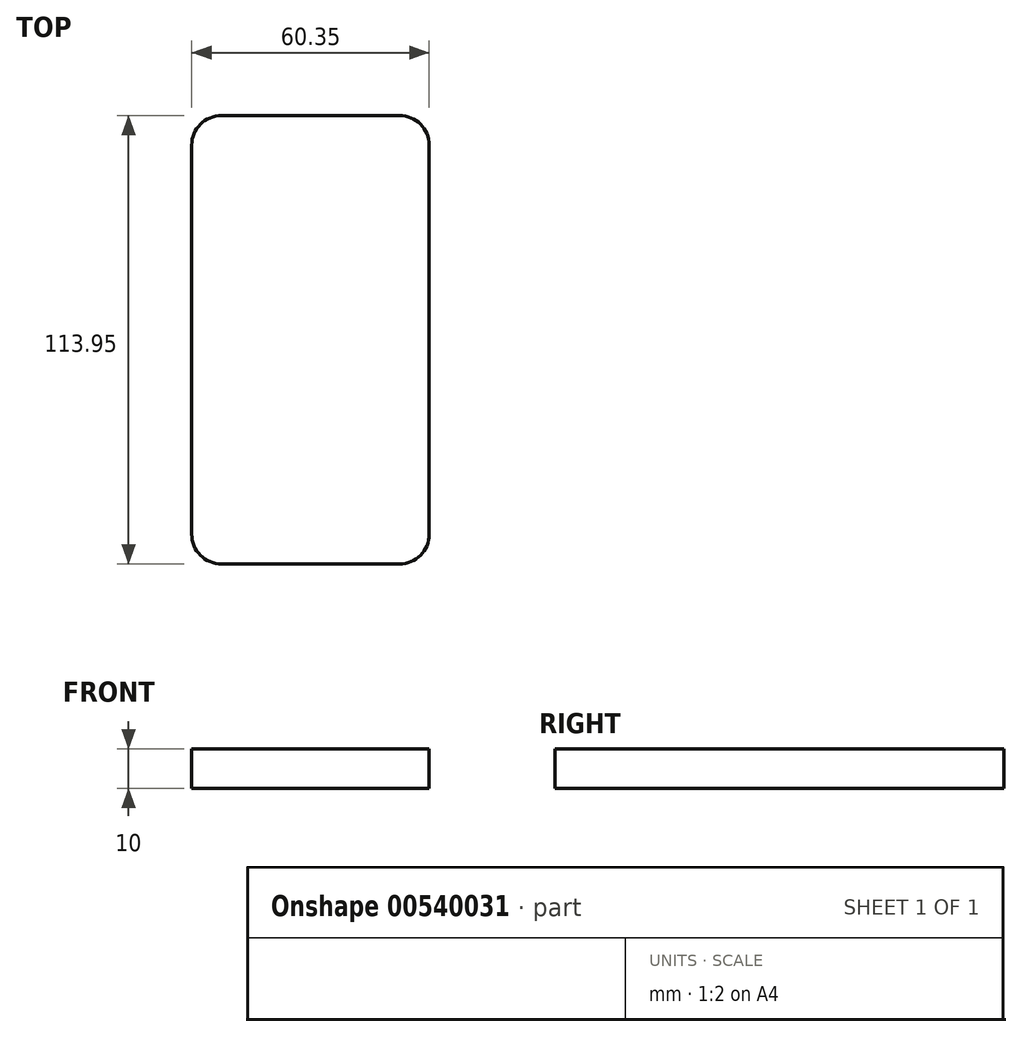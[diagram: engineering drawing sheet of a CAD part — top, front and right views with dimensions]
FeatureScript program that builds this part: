
annotation { "Feature Type Name" : "Feature", "Feature Type Description" : "" }
export const myFeature = defineFeature(function(context is Context, id is Id, definition is map)
    precondition{}
    {
        {
            var Q0;
            Q0=qCreatedBy(makeId("Top.planeOp"),FACE);
            var sketch = newSketch(context, id + "F0", { "sketchPlane" : qUnion([Q0])});
            skLineSegment(sketch, "E0.bottom", {"start": v(-64.28, 31.72) * mm, "end": v(-19.07, 31.72) * mm});
            skLineSegment(sketch, "E0.top", {"start": v(-64.28, -82.23) * mm, "end": v(-19.07, -82.23) * mm});
            skLineSegment(sketch, "E0.left", {"start": v(-71.85, 24.15) * mm, "end": v(-71.85, -74.66) * mm});
            skLineSegment(sketch, "E0.right", {"start": v(-11.5, 24.15) * mm, "end": v(-11.5, -74.66) * mm});
            skPoint(sketch, "E0.middle", {"position": v(-41.68, -25.25) * mm});
            skPoint(sketch, "E1.visualSharp", {"position": v(-71.85, 31.72) * mm});
            skArc(sketch, "E1.filletArc", {"start": v(-64.28, 31.72) * mm, "mid": v(-69.64, 29.5) * mm, "end": v(-71.85, 24.15) * mm});
            skPoint(sketch, "E2.visualSharp", {"position": v(-11.5, 31.72) * mm});
            skArc(sketch, "E2.filletArc", {"start": v(-11.5, 24.15) * mm, "mid": v(-13.72, 29.5) * mm, "end": v(-19.07, 31.72) * mm});
            skPoint(sketch, "E3.visualSharp", {"position": v(-71.85, -82.23) * mm});
            skArc(sketch, "E3.filletArc", {"start": v(-71.85, -74.66) * mm, "mid": v(-69.64, -80) * mm, "end": v(-64.28, -82.23) * mm});
            skPoint(sketch, "E4.visualSharp", {"position": v(-11.5, -82.23) * mm});
            skArc(sketch, "E4.filletArc", {"start": v(-19.07, -82.23) * mm, "mid": v(-13.72, -80) * mm, "end": v(-11.5, -74.66) * mm});
            skCircle(sketch, "E5", {"center": v(-41.68, -72.47) * mm, "radius": 5.6 * mm});
            skLineSegment(sketch, "E6.bottom", {"start": v(-37.43, 20.62) * mm, "end": v(-45.93, 20.62) * mm});
            skLineSegment(sketch, "E6.top", {"start": v(-37.43, 23.32) * mm, "end": v(-45.93, 23.32) * mm});
            skLineSegment(sketch, "E6.left", {"start": v(-36.08, 21.97) * mm, "end": v(-36.08, 21.97) * mm});
            skLineSegment(sketch, "E6.right", {"start": v(-47.28, 21.97) * mm, "end": v(-47.28, 21.97) * mm});
            skPoint(sketch, "E6.middle", {"position": v(-41.68, 21.97) * mm});
            skPoint(sketch, "E7.visualSharp", {"position": v(-47.28, 23.32) * mm});
            skArc(sketch, "E7.filletArc", {"start": v(-45.93, 23.32) * mm, "mid": v(-46.88, 22.93) * mm, "end": v(-47.28, 21.97) * mm});
            skPoint(sketch, "E8.visualSharp", {"position": v(-47.28, 20.62) * mm});
            skArc(sketch, "E8.filletArc", {"start": v(-47.28, 21.97) * mm, "mid": v(-46.88, 21.02) * mm, "end": v(-45.93, 20.62) * mm});
            skPoint(sketch, "E9.visualSharp", {"position": v(-36.08, 20.62) * mm});
            skArc(sketch, "E9.filletArc", {"start": v(-37.43, 20.62) * mm, "mid": v(-36.47, 21.02) * mm, "end": v(-36.08, 21.97) * mm});
            skPoint(sketch, "E10.visualSharp", {"position": v(-36.08, 23.32) * mm});
            skArc(sketch, "E10.filletArc", {"start": v(-36.08, 21.97) * mm, "mid": v(-36.47, 22.93) * mm, "end": v(-37.43, 23.32) * mm});
            skPoint(sketch, "E11.endSnap0", {"position": v(-41.68, 20.62) * mm});
            skPoint(sketch, "E12.middle", {"position": v(-41.68, 26.07) * mm});
            skLineSegment(sketch, "E13.left", {"start": v(-38.75, 26.07) * mm, "end": v(-38.75, 26.07) * mm});
            skLineSegment(sketch, "E14.MirrorCS", {"start": v(-44.6, 26.07) * mm, "end": v(-44.6, 26.07) * mm});
            skLineSegment(sketch, "E15", {"start": v(-44, 26.67) * mm, "end": v(-39.35, 26.67) * mm});
            skLineSegment(sketch, "E16", {"start": v(-39.35, 25.47) * mm, "end": v(-44, 25.47) * mm});
            skPoint(sketch, "E17.visualSharp", {"position": v(-44.6, 26.67) * mm});
            skArc(sketch, "E17.filletArc", {"start": v(-44, 26.67) * mm, "mid": v(-44.43, 26.5) * mm, "end": v(-44.6, 26.07) * mm});
            skPoint(sketch, "E18.visualSharp", {"position": v(-44.6, 25.47) * mm});
            skArc(sketch, "E18.filletArc", {"start": v(-44.6, 26.07) * mm, "mid": v(-44.43, 25.65) * mm, "end": v(-44, 25.47) * mm});
            skPoint(sketch, "E19.visualSharp", {"position": v(-38.75, 26.67) * mm});
            skArc(sketch, "E19.filletArc", {"start": v(-38.75, 26.07) * mm, "mid": v(-38.92, 26.5) * mm, "end": v(-39.35, 26.67) * mm});
            skPoint(sketch, "E20.visualSharp", {"position": v(-38.75, 25.47) * mm});
            skArc(sketch, "E20.filletArc", {"start": v(-39.35, 25.47) * mm, "mid": v(-38.92, 25.65) * mm, "end": v(-38.75, 26.07) * mm});
            skLineSegment(sketch, "E21.bottom", {"start": v(-66.64, 12.19) * mm, "end": v(-16.72, 12.19) * mm});
            skLineSegment(sketch, "E21.top", {"start": v(-66.64, -62.7) * mm, "end": v(-16.72, -62.7) * mm});
            skLineSegment(sketch, "E21.left", {"start": v(-66.64, 12.19) * mm, "end": v(-66.64, -62.7) * mm});
            skLineSegment(sketch, "E21.right", {"start": v(-16.72, 12.19) * mm, "end": v(-16.72, -62.7) * mm});
            skSolve(sketch);
        }
        {
            var Q0;
            Q0=sQuery(id+"F0.wireOp",EDGE,"E0.left");
            var Q1;
            Q1=sQuery(id+"F0.wireOp",EDGE,"E0.bottom");
            var Q2;
            Q2=sQuery(id+"F0.wireOp",EDGE,"E1.filletArc");
            var Q3;
            Q3=sQuery(id+"F0.wireOp",EDGE,"E2.filletArc");
            var Q4;
            Q4=sQuery(id+"F0.wireOp",EDGE,"E0.right");
            var Q5;
            Q5=sQuery(id+"F0.wireOp",EDGE,"E4.filletArc");
            var Q6;
            Q6=sQuery(id+"F0.wireOp",EDGE,"E3.filletArc");
            var Q7;
            Q7=sQuery(id+"F0.wireOp",EDGE,"E0.top");
            extrude(context, id + "F1", {"bodyType" : ToolBodyType.SURFACE, "surfaceEntities" : qUnion([Q0, Q1, Q2, Q3, Q4, Q5, Q6, Q7]), "depth" : 10 * mm, "offsetDistance" : 25 * mm});
        }
    });
